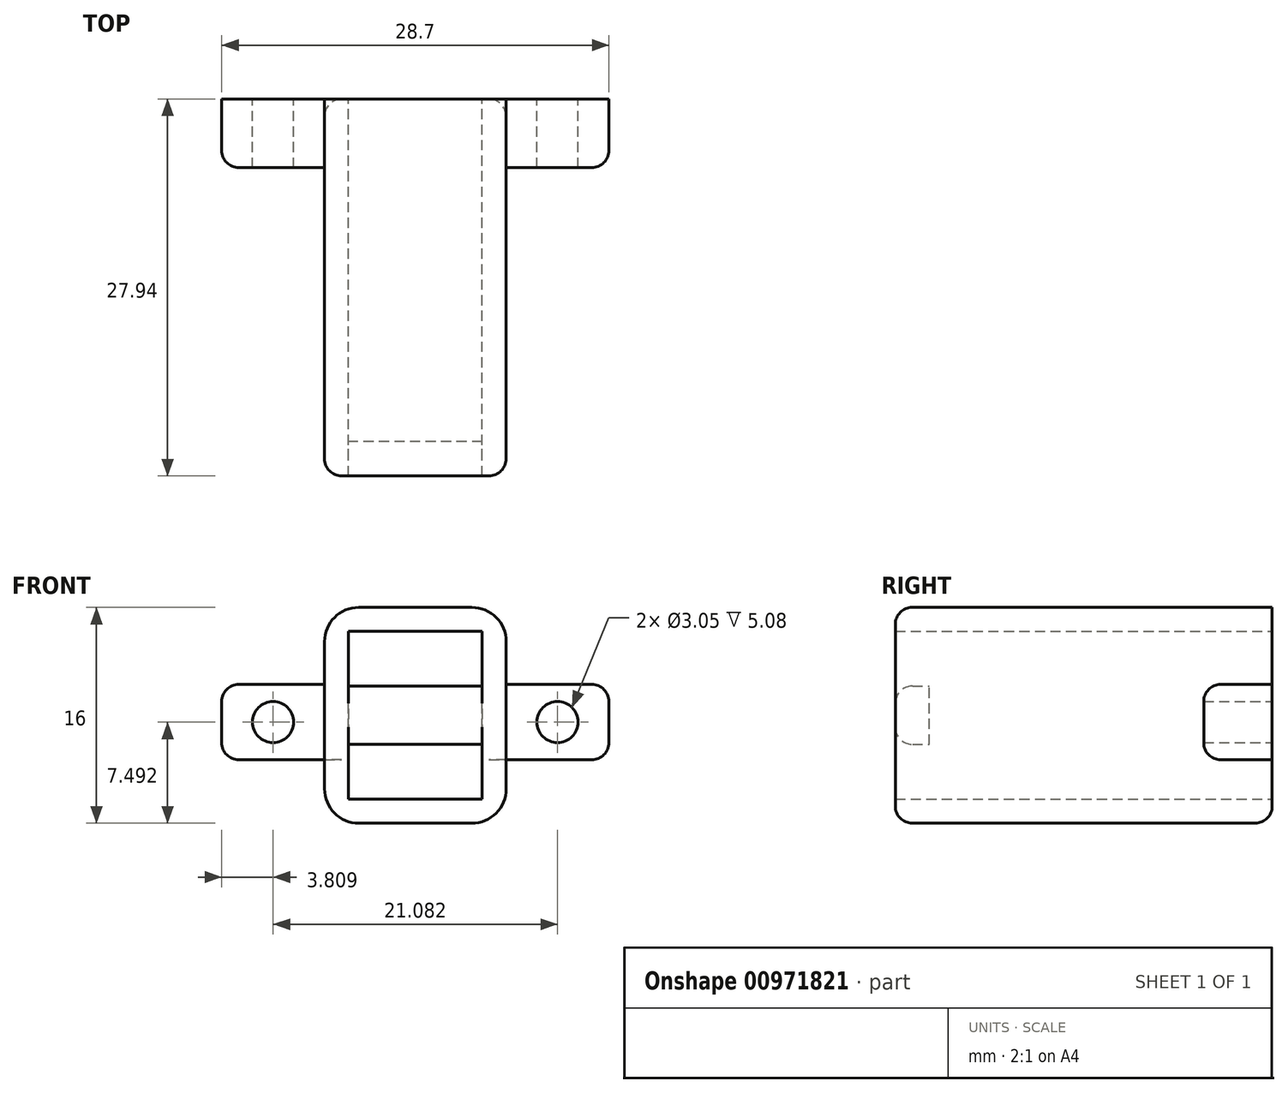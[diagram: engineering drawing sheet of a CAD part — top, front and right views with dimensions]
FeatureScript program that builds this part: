
annotation { "Feature Type Name" : "Feature", "Feature Type Description" : "" }
export const myFeature = defineFeature(function(context is Context, id is Id, definition is map)
    precondition{}
    {
        {
            var Q0;
            Q0=qCreatedBy(makeId("Front.planeOp"),FACE);
            var sketch = newSketch(context, id + "F0", { "sketchPlane" : qUnion([Q0])});
            skLineSegment(sketch, "E0.bottom", {"start": v(-6.73, 8) * mm, "end": v(6.73, 8) * mm});
            skLineSegment(sketch, "E0.top", {"start": v(-6.73, -8) * mm, "end": v(6.73, -8) * mm});
            skLineSegment(sketch, "E0.left", {"start": v(-6.73, 8) * mm, "end": v(-6.73, -8) * mm});
            skLineSegment(sketch, "E0.right", {"start": v(6.73, 8) * mm, "end": v(6.73, -8) * mm});
            skPoint(sketch, "E0.middle", {"position": v(0, 0) * mm});
            skLineSegment(sketch, "E1.bottom", {"start": v(4.95, -2.16) * mm, "end": v(-4.95, -2.16) * mm});
            skLineSegment(sketch, "E1.top", {"start": v(4.95, 2.16) * mm, "end": v(-4.95, 2.16) * mm});
            skLineSegment(sketch, "E1.left", {"start": v(4.95, -2.16) * mm, "end": v(4.95, 2.16) * mm});
            skLineSegment(sketch, "E1.right", {"start": v(-4.95, -2.16) * mm, "end": v(-4.95, 2.16) * mm});
            skPoint(sketch, "E2", {"position": v(6.73, 0) * mm});
            skPoint(sketch, "E3", {"position": v(10.54, -0.5) * mm});
            skLineSegment(sketch, "E4.bottom", {"start": v(6.73, -3.3) * mm, "end": v(14.35, -3.3) * mm});
            skLineSegment(sketch, "E4.top", {"start": v(6.73, 2.29) * mm, "end": v(14.35, 2.29) * mm});
            skLineSegment(sketch, "E4.left", {"start": v(6.73, -3.3) * mm, "end": v(6.73, 2.29) * mm});
            skLineSegment(sketch, "E4.right", {"start": v(14.35, -3.3) * mm, "end": v(14.35, 2.29) * mm});
            skLineSegment(sketch, "E5", {"start": v(0, 0) * mm, "end": v(0, -1.27) * mm});
            skLineSegment(sketch, "E6.MirrorCS", {"start": v(-6.73, 2.29) * mm, "end": v(-14.35, 2.29) * mm});
            skLineSegment(sketch, "E7.MirrorCS", {"start": v(-14.35, -3.3) * mm, "end": v(-14.35, 2.29) * mm});
            skLineSegment(sketch, "E8.MirrorCS", {"start": v(-6.73, -3.3) * mm, "end": v(-14.35, -3.3) * mm});
            skPoint(sketch, "E9.MirrorP", {"position": v(-10.54, -0.5) * mm});
            skSolve(sketch);
        }
        {
            var Q0;
            Q0=makeQuery(id+"F0.imprint","IMPRINT",FACE,{"disambiguationData":[TD([[makeQuery(id+"F0.imprint","IMPRINT",EDGE,{"derivedFrom":sQuery(id+"F0.wireOp",EDGE,"E1.bottom")}),-1.0]])]});
            var Q1;
            Q1=makeQuery(id+"F0.imprint","IMPRINT",FACE,{"disambiguationData":[TD([[makeQuery(id+"F0.imprint","IMPRINT",EDGE,{"derivedFrom":sQuery(id+"F0.wireOp",EDGE,"E0.bottom")}),-1.0]])]});
            extrude(context, id + "F1", {"entities" : qUnion([Q0, Q1]), "depth" : 27.94 * mm, "offsetDistance" : 25.4 * mm});
        }
        {
            var Q0;
            Q0=makeQuery(id+"F1.opExtrude","CAP_FACE",FACE,{"disambiguationData":[OSD([sQuery(id+"F0.wireOp",EDGE,"E0.bottom"),sQuery(id+"F0.wireOp",EDGE,"E0.top"),sQuery(id+"F0.wireOp",EDGE,"E0.left"),sQuery(id+"F0.wireOp",EDGE,"E0.right")])],"isStart":false});
            var Q1;
            Q1=makeQuery(id+"F1.opExtrude","CAP_FACE",FACE,{"disambiguationData":[OSD([sQuery(id+"F0.wireOp",EDGE,"E0.bottom"),sQuery(id+"F0.wireOp",EDGE,"E0.top"),sQuery(id+"F0.wireOp",EDGE,"E0.left"),sQuery(id+"F0.wireOp",EDGE,"E0.right")])],"isStart":true});
            shell(context, id + "F2", {"entities" : qUnion([Q0, Q1]), "thickness" : 1.78 * mm});
        }
        {
            var Q0;
            Q0=makeQuery(id+"F0.imprint","IMPRINT",FACE,{"disambiguationData":[TD([[makeQuery(id+"F0.imprint","IMPRINT",EDGE,{"derivedFrom":sQuery(id+"F0.wireOp",EDGE,"E1.bottom")}),-1.0]])]});
            extrude(context, id + "F3", {"entities" : qUnion([Q0]), "operationType" : NewBodyOperationType.ADD, "depth" : 27.94 * mm, "offsetDistance" : 25.4 * mm});
        }
        {
            var Q0;
            Q0=makeQuery(id+"F0.imprint","IMPRINT",FACE,{"disambiguationData":[TD([[makeQuery(id+"F0.imprint","IMPRINT",EDGE,{"derivedFrom":sQuery(id+"F0.wireOp",EDGE,"E1.bottom")}),-1.0]])]});
            extrude(context, id + "F4", {"entities" : qUnion([Q0]), "operationType" : NewBodyOperationType.REMOVE, "depth" : 25.4 * mm, "offsetDistance" : 25.4 * mm});
        }
        {
            var Q0;
            {var subQ0=sQuery(id+"F0.wireOp",EDGE,"E6.MirrorCS");Q0=makeQuery(id+"F0.imprint","IMPRINT",FACE,{"disambiguationData":[TD([[makeQuery(id+"F0.imprint","IMPRINT",EDGE,{"derivedFrom":subQ0}),1.0]])]});}
            var Q1;
            Q1=makeQuery(id+"F0.imprint","IMPRINT",FACE,{"disambiguationData":[TD([[makeQuery(id+"F0.imprint","IMPRINT",EDGE,{"derivedFrom":sQuery(id+"F0.wireOp",EDGE,"E4.bottom")}),1.0]])]});
            extrude(context, id + "F5", {"entities" : qUnion([Q0, Q1]), "operationType" : NewBodyOperationType.ADD, "depth" : 5.08 * mm, "offsetDistance" : 25.4 * mm});
        }
        {
            var Q0;
            Q0=makeQuery(id+"F1.opExtrude","SWEPT_EDGE",EDGE,{"disambiguationData":[OSD([sQuery(id+"F0.wireOp",EDGE,"E0.bottom"),sQuery(id+"F0.wireOp",EDGE,"E0.right")])]});
            var Q1;
            Q1=makeQuery(id+"F1.opExtrude","SWEPT_EDGE",EDGE,{"disambiguationData":[OSD([sQuery(id+"F0.wireOp",EDGE,"E0.bottom"),sQuery(id+"F0.wireOp",EDGE,"E0.left")])]});
            var Q2;
            Q2=makeQuery(id+"F1.opExtrude","SWEPT_EDGE",EDGE,{"disambiguationData":[OSD([sQuery(id+"F0.wireOp",EDGE,"E0.top"),sQuery(id+"F0.wireOp",EDGE,"E0.right")])]});
            var Q3;
            Q3=makeQuery(id+"F1.opExtrude","SWEPT_EDGE",EDGE,{"disambiguationData":[OSD([sQuery(id+"F0.wireOp",EDGE,"E0.top"),sQuery(id+"F0.wireOp",EDGE,"E0.left")])]});
            fillet(context, id + "F6", {"entities" : qUnion([Q0, Q1, Q2, Q3]), "radius" : 2.54 * mm, "tangentPropagation" : true, "allowEdgeOverflow" : false});
        }
        {
            var Q0;
            Q0=makeQuery(id+"F5.opExtrude","SWEPT_EDGE",EDGE,{"disambiguationData":[OSD([sQuery(id+"F0.wireOp",EDGE,"E4.top"),sQuery(id+"F0.wireOp",EDGE,"E4.right")])]});
            var Q1;
            Q1=makeQuery(id+"F5.opExtrude","SWEPT_EDGE",EDGE,{"disambiguationData":[OSD([sQuery(id+"F0.wireOp",EDGE,"E4.bottom"),sQuery(id+"F0.wireOp",EDGE,"E4.right")])]});
            var Q2;
            Q2=makeQuery(id+"F5.opExtrude","SWEPT_EDGE",EDGE,{"disambiguationData":[OSD([sQuery(id+"F0.wireOp",EDGE,"E6.MirrorCS"),sQuery(id+"F0.wireOp",EDGE,"E7.MirrorCS")])]});
            var Q3;
            Q3=makeQuery(id+"F5.opExtrude","SWEPT_EDGE",EDGE,{"disambiguationData":[OSD([sQuery(id+"F0.wireOp",EDGE,"E7.MirrorCS"),sQuery(id+"F0.wireOp",EDGE,"E8.MirrorCS")])]});
            var Q4;
            Q4=makeQuery(id+"F5.opExtrude","CAP_EDGE",EDGE,{"disambiguationData":[OSD([sQuery(id+"F0.wireOp",EDGE,"E7.MirrorCS")])],"isStart":false});
            var Q5;
            Q5=makeQuery(id+"F5.opExtrude","CAP_EDGE",EDGE,{"disambiguationData":[OSD([sQuery(id+"F0.wireOp",EDGE,"E6.MirrorCS")])],"isStart":false});
            var Q6;
            Q6=makeQuery(id+"F5.opExtrude","CAP_EDGE",EDGE,{"disambiguationData":[OSD([sQuery(id+"F0.wireOp",EDGE,"E8.MirrorCS")])],"isStart":false});
            var Q7;
            Q7=makeQuery(id+"F5.opExtrude","SWEPT_EDGE",EDGE,{"disambiguationData":[OSD([sQuery(id+"F0.wireOp",EDGE,"E0.left"),sQuery(id+"F0.wireOp",EDGE,"E6.MirrorCS")])]});
            var Q8;
            Q8=makeQuery(id+"F5.opExtrude","SWEPT_EDGE",EDGE,{"disambiguationData":[OSD([sQuery(id+"F0.wireOp",EDGE,"E0.right"),sQuery(id+"F0.wireOp",EDGE,"E4.top"),sQuery(id+"F0.wireOp",EDGE,"E4.left")])]});
            var Q9;
            Q9=makeQuery(id+"F5.opExtrude","CAP_EDGE",EDGE,{"disambiguationData":[OSD([sQuery(id+"F0.wireOp",EDGE,"E4.left")])],"isStart":false});
            var Q10;
            Q10=makeQuery(id+"F5.opExtrude","SWEPT_EDGE",EDGE,{"disambiguationData":[OSD([sQuery(id+"F0.wireOp",EDGE,"E0.right"),sQuery(id+"F0.wireOp",EDGE,"E4.bottom"),sQuery(id+"F0.wireOp",EDGE,"E4.left")])]});
            var Q11;
            Q11=makeQuery(id+"F5.opExtrude","CAP_EDGE",EDGE,{"disambiguationData":[OSD([sQuery(id+"F0.wireOp",EDGE,"E4.right")])],"isStart":false});
            var Q12;
            Q12=makeQuery(id+"F5.opExtrude","CAP_EDGE",EDGE,{"disambiguationData":[OSD([sQuery(id+"F0.wireOp",EDGE,"E4.top")])],"isStart":false});
            var Q13;
            Q13=makeQuery(id+"F5.opExtrude","CAP_EDGE",EDGE,{"disambiguationData":[OSD([sQuery(id+"F0.wireOp",EDGE,"E4.bottom")])],"isStart":false});
            fillet(context, id + "F7", {"entities" : qUnion([Q0, Q1, Q2, Q3, Q4, Q5, Q6, Q7, Q8, Q9, Q10, Q11, Q12, Q13]), "radius" : 1.27 * mm, "tangentPropagation" : true, "allowEdgeOverflow" : false});
        }
        {
            var Q0;
            Q0=sQuery(id+"F0.wireOp",VERTEX,"E3");
            var Q1;
            Q1=sQuery(id+"F0.wireOp",VERTEX,"E9.MirrorP");
            var Q2;
            Q2=makeQuery(id+"F1.opExtrude","SWEPT_BODY",BODY,{"disambiguationData":[OSD([sQuery(id+"F0.wireOp",EDGE,"E0.bottom"),sQuery(id+"F0.wireOp",EDGE,"E0.top"),sQuery(id+"F0.wireOp",EDGE,"E0.left"),sQuery(id+"F0.wireOp",EDGE,"E0.right"),sQuery(id+"F0.wireOp",EDGE,"E4.left")])]});
            hole(context, id + "F8", {"style" : HoleStyle.SIMPLE, "endStyle" : HoleEndStyle.THROUGH, "oppositeDirection" : true, "holeDiameter" : 3.05 * mm, "majorDiameter" : 6.35 * mm, "isTappedThrough" : true, "tappedDepth" : 12.7 * mm, "tapClearance" : 3, "locations" : qUnion([Q0, Q1]), "scope" : qUnion([Q2])});
        }
        {
            var Q0;
            Q0=makeQuery(id+"F1.opExtrude","CAP_EDGE",EDGE,{"disambiguationData":[OSD([sQuery(id+"F0.wireOp",EDGE,"E0.top")])],"isStart":false});
            var Q1;
            Q1=makeQuery(id+"F3.opExtrude","CAP_EDGE",EDGE,{"disambiguationData":[OSD([sQuery(id+"F0.wireOp",EDGE,"E1.bottom")])],"isStart":false});
            var Q2;
            Q2=makeQuery(id+"F3.opExtrude","CAP_EDGE",EDGE,{"disambiguationData":[OSD([sQuery(id+"F0.wireOp",EDGE,"E1.top")])],"isStart":false});
            var Q3;
            Q3=makeQuery(id+"F1.opExtrude","CAP_EDGE",EDGE,{"disambiguationData":[OSD([sQuery(id+"F0.wireOp",EDGE,"E0.top")])],"isStart":true});
            fillet(context, id + "F9", {"entities" : qUnion([Q0, Q1, Q2, Q3]), "radius" : 1.27 * mm, "tangentPropagation" : true, "allowEdgeOverflow" : false});
        }
    });
